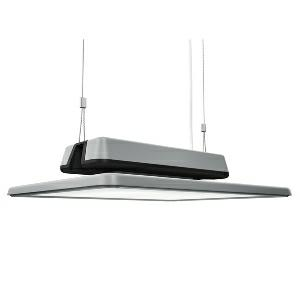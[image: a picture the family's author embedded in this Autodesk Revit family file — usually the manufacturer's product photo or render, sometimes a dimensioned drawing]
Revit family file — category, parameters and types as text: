
# Revit family: acaneo_-_hial_30000_840_n_ea_00734099_e06b
name_source: partatom
category: Lighting Fixtures
units: mm (PartAtom-declared; Revit-internal decimal feet)

## family parameters
Cut with Voids When Loaded = No
Host = Face
Light Source = No
Part Type = Normal
Room Calculation Point = No
Round Connector Dimension = Use Diameter
Shared = No

## types (1)
- ACANEO - HIAL 30000/840/N/EA (1 x LED, 33000 lm, 4000K)
    Apparent Load = 206 VA
    Approval mark = CE
    CIE Flux Codes = 84 97 100 100 100
    Color Rendering = 80-89
    Color Temperature = 4000K
    Control Gear = Electronic ballast
    Default Elevation = 1800 mm
    Description = HIAL 30000/840/N/EA|High bay luminaire|light source: LED|work equipment: Electronic ballast|connected load: 220-240 V, 50/60 Hz|Power consumption: approx. 206 W|power factor: approx. 0,973|luminous flux: 33000 lm|luminous efficacy: 160 lm/W|colour temperature: Cold white, ca. 4000 K|color rendering index (CRI): >= 80|chromaticity tolerance:  3 SDCM|System of protection: IP 65|class of protection: I|technology: Switchable|luminaire body|material: Aluminium|surface: Powder coatet|colour: White aluminium|lamp cover: Acrylic (PMMA), Clear|weight (net): approx. 10.8 kg|mains lead: Built-in plug RST 25i3 Einbau|Fastening: Available separately|Accessory: Junction box (RST 2013)|minimum ambient temperature: -30 ░C|maximum ambient temperature: 50 ░C|glare control: Optics|unified glare rating(4H 8H): <=  22|
    Frequency = 50 Hz, 60 Hz
    Height = 125 mm
    Lamp = 1 x LED
    Lamp Light Flux = 33000 lm
    Lamp count = 1
    Length = 585 mm
    Luminous efficacy = 160 lm/W
    Manufacturer = Waldmann
    ModVariant = No
    Model = 00734099
    Mounting Place = Ceiling
    Mounting Type = Pendant
    Number of Poles = 1
    OnlyDefault = Yes
    Power Factor = 1
    Product Name = ACANEO - HIAL 30000/840/N/EA
    Product group = High bay luminaire (industry)
    ProductGroupID = 901
    Protection Class = Protection class I
    Protection Degree = IP 65
    RLX_Detail_Level = 1
    RLX_Emergency_Light_Flux = 0 lm
    RLX_Emergency_Type = 0
    RLX_Emergency_Type_DB = No
    RlxData = <blob elided: 29821 chars, md5=3719ab13>
    Socket = socket
    Standby Power = 0 W
    System Light Flux = 32999 lm
    System Power = 206 W
    Type Comments = Product without accessories
    Type Image = acaneo-hial.jpg
    URL = http://relux.com
    VarID = ---
    Voltage = 230 V
    Voltage Range = 110-120 V, 220-240 V
    Weight = 0.00 kg
    Width = 480 mm

## geometry (parser evidence)
native form markers: Blend x4, Sweep x11
no freeform markers — native parametric forms only
